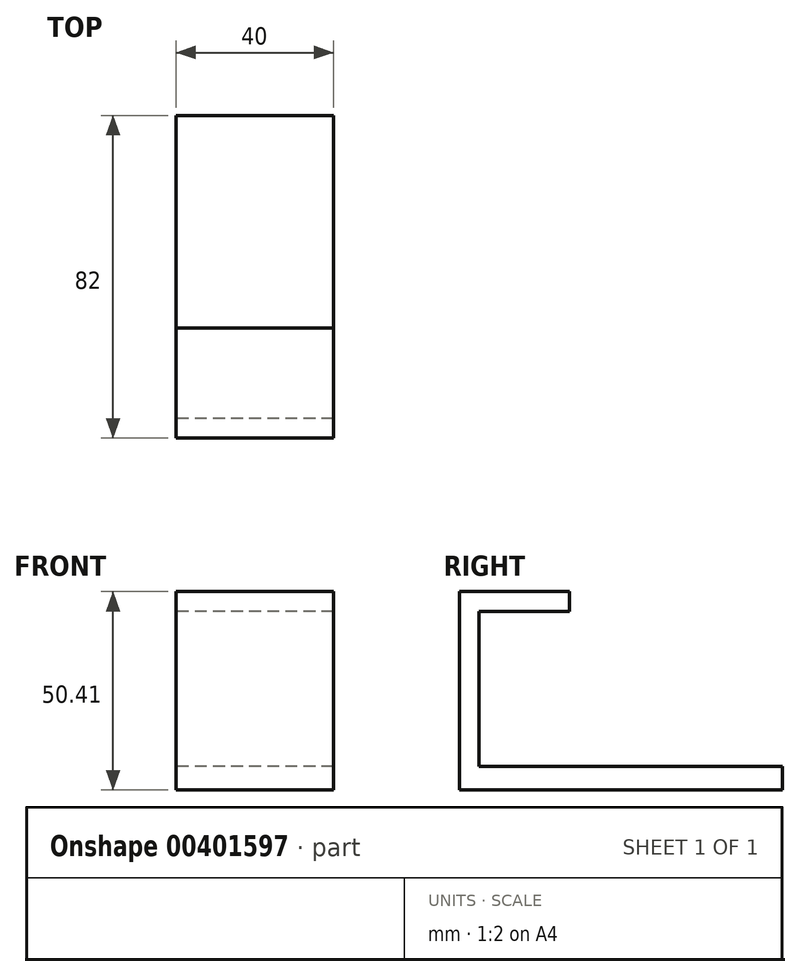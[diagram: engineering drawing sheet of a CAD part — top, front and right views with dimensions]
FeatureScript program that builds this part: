
annotation { "Feature Type Name" : "Feature", "Feature Type Description" : "" }
export const myFeature = defineFeature(function(context is Context, id is Id, definition is map)
    precondition{}
    {
        {
            var Q0;
            Q0=qCreatedBy(makeId("Right.planeOp"),FACE);
            var sketch = newSketch(context, id + "F0", { "sketchPlane" : qUnion([Q0])});
            skLineSegment(sketch, "E0", {"start": v(-25, -6) * mm, "end": v(-25, 44.41) * mm});
            skLineSegment(sketch, "E1", {"start": v(-20, 39.41) * mm, "end": v(-20, 0) * mm});
            skLineSegment(sketch, "E2", {"start": v(-20, 0) * mm, "end": v(57, 0) * mm});
            skLineSegment(sketch, "E3", {"start": v(57, 0) * mm, "end": v(57, -6) * mm});
            skLineSegment(sketch, "E4", {"start": v(-25, 44.41) * mm, "end": v(3, 44.41) * mm});
            skLineSegment(sketch, "E5", {"start": v(-20, 39.41) * mm, "end": v(3, 39.41) * mm});
            skLineSegment(sketch, "E6", {"start": v(3, 44.41) * mm, "end": v(3, 39.41) * mm});
            skLineSegment(sketch, "E7", {"start": v(57, -6) * mm, "end": v(-25, -6) * mm});
            skSolve(sketch);
        }
        {
            var Q0;
            Q0=makeQuery(id+"F0.imprint","IMPRINT",FACE,{"disambiguationData":[TD([[makeQuery(id+"F0.imprint","IMPRINT",EDGE,{"derivedFrom":sQuery(id+"F0.wireOp",EDGE,"E0")}),-1.0]])]});
            extrude(context, id + "F1", {"entities" : qUnion([Q0]), "depth" : 40 * mm});
        }
    });
